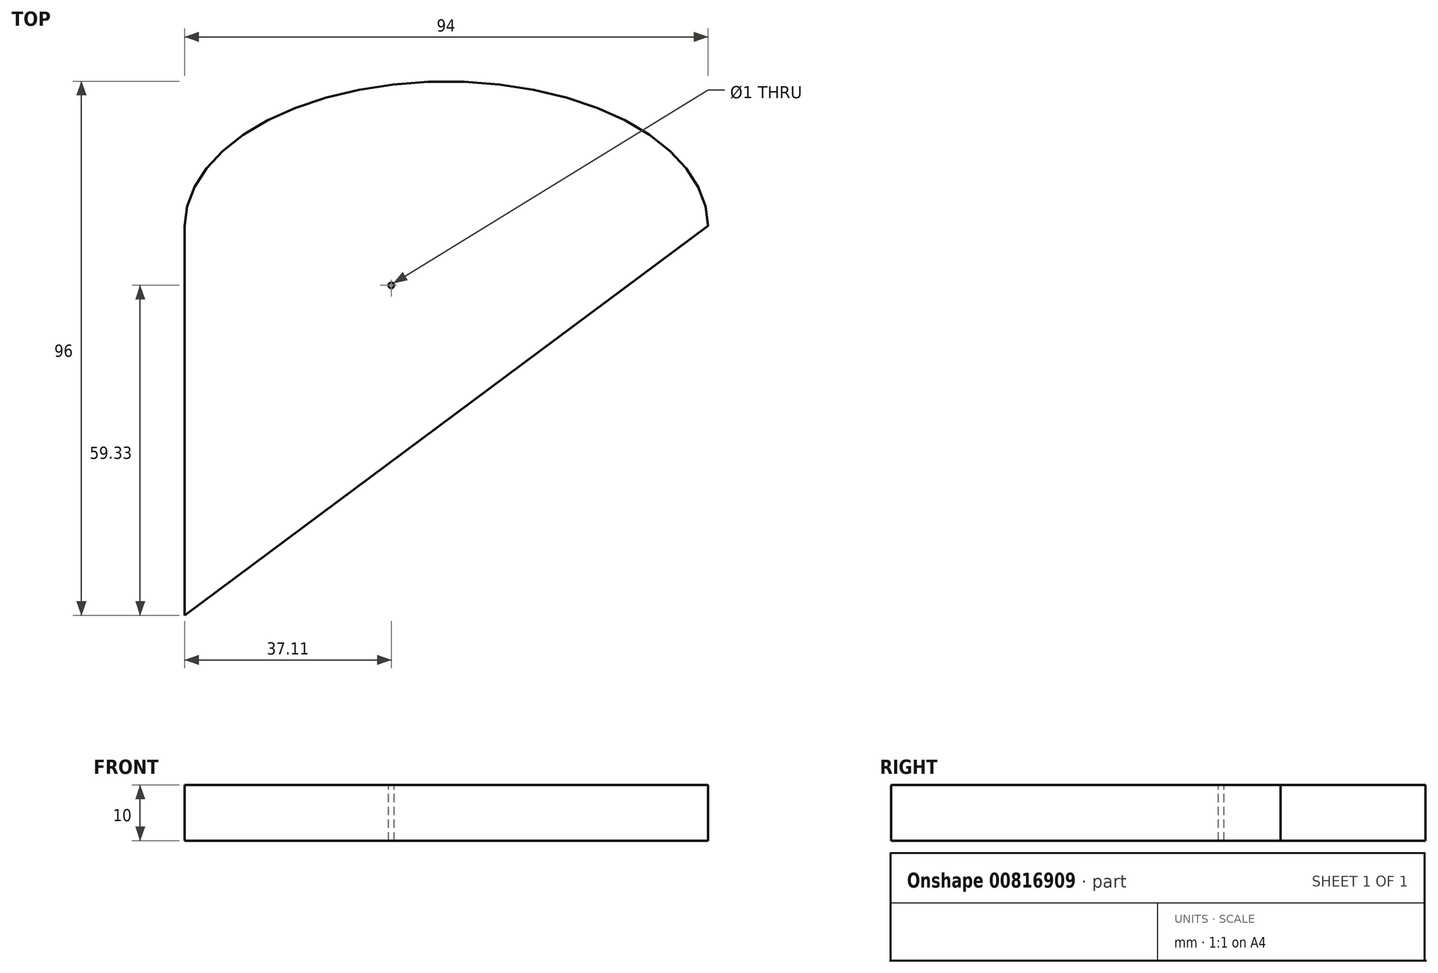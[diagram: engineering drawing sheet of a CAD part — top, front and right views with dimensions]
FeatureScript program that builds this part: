
annotation { "Feature Type Name" : "Feature", "Feature Type Description" : "" }
export const myFeature = defineFeature(function(context is Context, id is Id, definition is map)
    precondition{}
    {
        {
            var Q0;
            Q0=qCreatedBy(makeId("Top.planeOp"),FACE);
            var sketch = newSketch(context, id + "F0", { "sketchPlane" : qUnion([Q0])});
            skLineSegment(sketch, "E0.bottom", {"start": v(47, 70) * mm, "end": v(-47, 70) * mm});
            skLineSegment(sketch, "E0.top", {"start": v(47, -70) * mm, "end": v(-47, -70) * mm});
            skLineSegment(sketch, "E0.left", {"start": v(47, 70) * mm, "end": v(47, -70) * mm});
            skLineSegment(sketch, "E0.right", {"start": v(-47, 70) * mm, "end": v(-47, -70) * mm});
            skPoint(sketch, "E0.middle", {"position": v(0, 0) * mm});
            skLineSegment(sketch, "E1", {"start": v(-47, -70) * mm, "end": v(47, 0) * mm});
            skEllipse(sketch, "E2", {"center": v(0, 0) * mm, "majorRadius": 47 * mm, "minorRadius": 26 * mm, "majorAxis": v(1, 0)});
            skPoint(sketch, "E3", {"position": v(-9.9, 0) * mm});
            skPoint(sketch, "E4", {"position": v(-9.9, -10.67) * mm});
            skSolve(sketch);
        }
        {
            var Q0;
            {var subQ0=sQuery(id+"F0.wireOp",EDGE,"E2");var subQ4=makeQuery(id+"F0.imprint","INTERSECT",VERTEX,{"derivedFrom":[sQuery(id+"F0.wireOp",EDGE,"E0.right"),subQ0]});Q0=makeQuery(id+"F0.imprint","IMPRINT",FACE,{"disambiguationData":[TD([[makeQuery(id+"F0.imprint","IMPRINT",EDGE,{"disambiguationData":[TD([[subQ4,-1.0]])],"derivedFrom":subQ0}),1.0]])]});}
            var Q1;
            {var subQ1=sQuery(id+"F0.wireOp",EDGE,"E0.right");var subQ3=sQuery(id+"F0.wireOp",EDGE,"E2");var subQ4=makeQuery(id+"F0.imprint","INTERSECT",VERTEX,{"derivedFrom":[subQ1,subQ3]});Q1=makeQuery(id+"F0.imprint","IMPRINT",FACE,{"disambiguationData":[TD([[makeQuery(id+"F0.imprint","IMPRINT",EDGE,{"disambiguationData":[TD([[subQ4,-1.0]])],"derivedFrom":subQ3}),-1.0]])]});}
            extrude(context, id + "F1", {"entities" : qUnion([Q0, Q1]), "depth" : 10 * mm, "offsetDistance" : 25 * mm});
        }
        {
            var Q0;
            Q0=makeQuery(id+"F1.opExtrude","CAP_FACE",FACE,{"disambiguationData":[OSD([sQuery(id+"F0.wireOp",EDGE,"E0.right"),sQuery(id+"F0.wireOp",EDGE,"E1"),sQuery(id+"F0.wireOp",EDGE,"E2")])],"isStart":false});
            var sketch = newSketch(context, id + "F2", { "sketchPlane" : qUnion([Q0])});
            skLineSegment(sketch, "E5", {"start": v(0, 0) * mm, "end": v(-9.9, 0) * mm});
            skLineSegment(sketch, "E6", {"start": v(-9.9, 0) * mm, "end": v(-9.9, -10.67) * mm});
            skCircle(sketch, "E7", {"center": v(-9.9, -10.67) * mm, "radius": 0.5 * mm});
            skSolve(sketch);
        }
        {
            var Q0;
            Q0=makeQuery(id+"F2.imprint","IMPRINT",FACE,{"disambiguationData":[TD([[makeQuery(id+"F2.imprint","IMPRINT",EDGE,{"derivedFrom":sQuery(id+"F2.wireOp",EDGE,"E7")}),1.0]])]});
            extrude(context, id + "F3", {"entities" : qUnion([Q0]), "operationType" : NewBodyOperationType.REMOVE, "endBound" : BoundingType.THROUGH_ALL, "oppositeDirection" : true, "depth" : 25 * mm, "offsetDistance" : 25 * mm});
        }
    });
